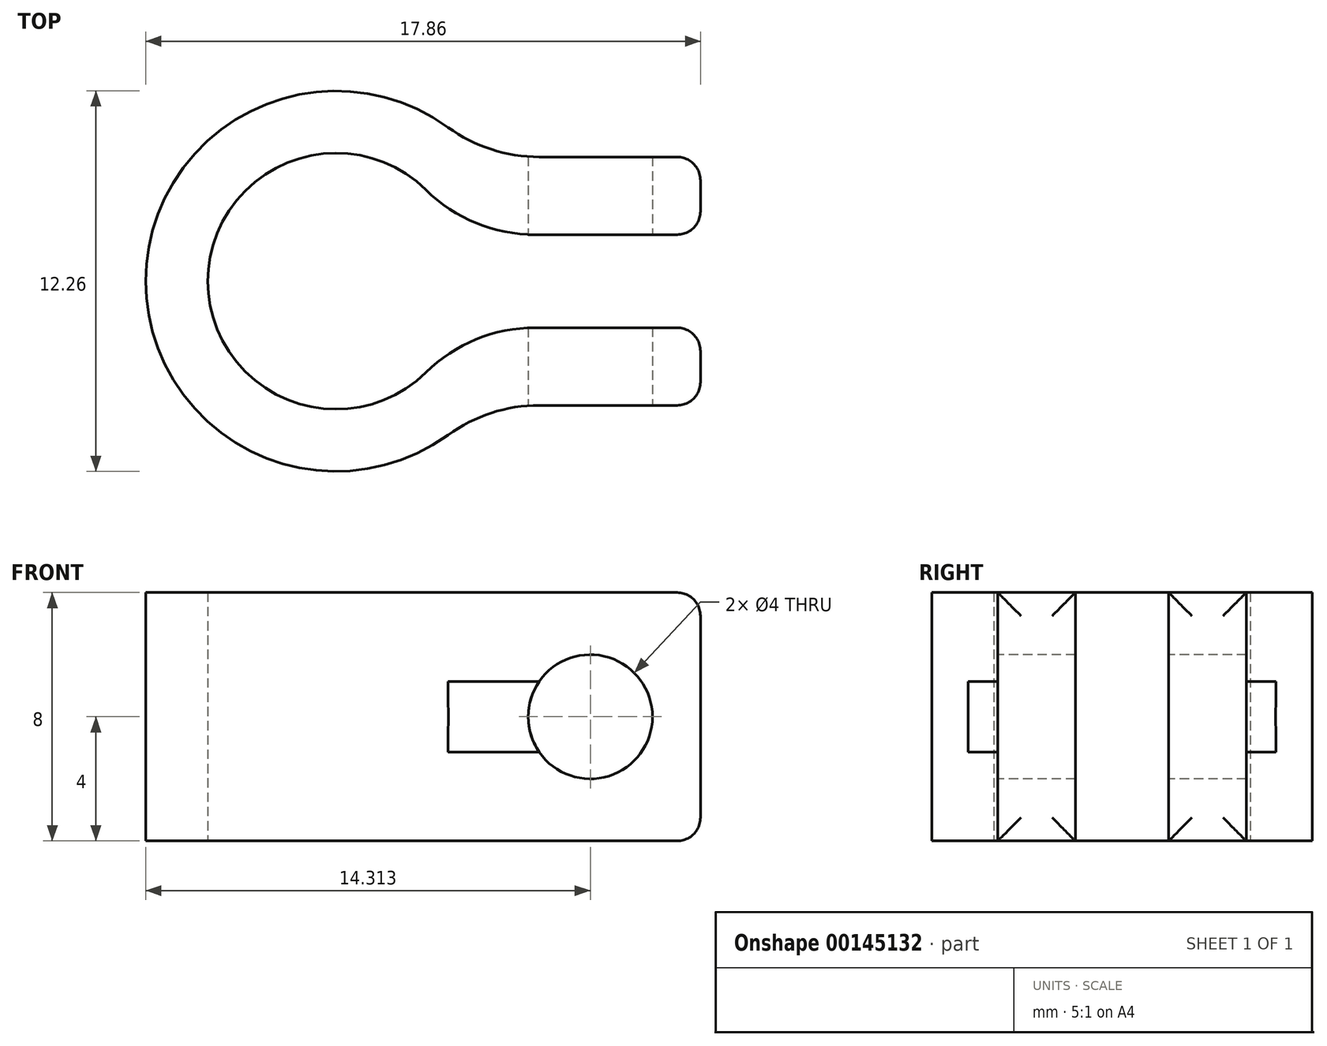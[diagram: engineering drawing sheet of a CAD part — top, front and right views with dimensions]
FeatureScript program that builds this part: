
annotation { "Feature Type Name" : "Feature", "Feature Type Description" : "" }
export const myFeature = defineFeature(function(context is Context, id is Id, definition is map)
    precondition{}
    {
        {
            var Q0;
            Q0=qCreatedBy(makeId("Top.planeOp"),FACE);
            var sketch = newSketch(context, id + "F0", { "sketchPlane" : qUnion([Q0])});
            skCircle(sketch, "E0", {"center": v(0, 0) * mm, "radius": 4.12 * mm});
            skCircle(sketch, "E1", {"center": v(0, 0) * mm, "radius": 6.12 * mm});
            skLineSegment(sketch, "E2.bottom", {"start": v(4.64, -4) * mm, "end": v(11.73, -4) * mm});
            skLineSegment(sketch, "E2.top", {"start": v(4.64, 4) * mm, "end": v(11.73, 4) * mm});
            skLineSegment(sketch, "E2.right", {"start": v(11.73, -4) * mm, "end": v(11.73, 4) * mm});
            skLineSegment(sketch, "E3", {"start": v(11.73, 0) * mm, "end": v(4.12, 0) * mm, "construction": true});
            skLineSegment(sketch, "E4.0", {"start": v(11.73, 1.5) * mm, "end": v(3.84, 1.5) * mm});
            skLineSegment(sketch, "E5.0", {"start": v(11.73, -1.5) * mm, "end": v(3.84, -1.5) * mm});
            skSolve(sketch);
        }
        {
            var Q0;
            {var subQ0=sQuery(id+"F0.wireOp",EDGE,"E2.top");Q0=makeQuery(id+"F0.imprint","IMPRINT",FACE,{"disambiguationData":[TD([[makeQuery(id+"F0.imprint","IMPRINT",EDGE,{"derivedFrom":subQ0}),-1.0]])]});}
            var Q1;
            {var subQ0=sQuery(id+"F0.wireOp",EDGE,"E2.bottom");Q1=makeQuery(id+"F0.imprint","IMPRINT",FACE,{"disambiguationData":[TD([[makeQuery(id+"F0.imprint","IMPRINT",EDGE,{"derivedFrom":subQ0}),1.0]])]});}
            var Q2;
            {var subQ5=sQuery(id+"F0.wireOp",EDGE,"E4.0");var subQ7=sQuery(id+"F0.wireOp",EDGE,"E0");var subQ8=makeQuery(id+"F0.imprint","INTERSECT",VERTEX,{"derivedFrom":[subQ7,subQ5]});Q2=makeQuery(id+"F0.imprint","IMPRINT",FACE,{"disambiguationData":[TD([[makeQuery(id+"F0.imprint","IMPRINT",EDGE,{"disambiguationData":[TD([[subQ8,-1.0]])],"derivedFrom":subQ7}),-1.0]])]});}
            extrude(context, id + "F1", {"entities" : qUnion([Q0, Q1, Q2]), "depth" : 8 * mm});
        }
        {
            var Q0;
            Q0=makeQuery(id+"F1.opExtrude","SWEPT_FACE",FACE,{"disambiguationData":[OSD([sQuery(id+"F0.wireOp",EDGE,"E2.bottom")])]});
            var sketch = newSketch(context, id + "F2", { "sketchPlane" : qUnion([Q0])});
            skCircle(sketch, "E6", {"center": v(8.18, 4) * mm, "radius": 2 * mm});
            skPoint(sketch, "E6.centerSnap0", {"position": v(8.18, 8) * mm});
            skPoint(sketch, "E6.centerSnap1", {"position": v(11.73, 4) * mm});
            skSolve(sketch);
        }
        {
            var Q0;
            Q0 = qSketchRegion(id + "F2", true);
            extrude(context, id + "F3", {"entities" : qUnion([Q0]), "operationType" : NewBodyOperationType.REMOVE, "oppositeDirection" : true, "depth" : 25 * mm});
        }
        {
            var Q0;
            {var subQ0=sQuery(id+"F0.wireOp",EDGE,"E2.right");Q0=makeQuery(id+"F1.opExtrude","CAP_EDGE",EDGE,{"disambiguationData":[OSD([subQ0]),TDD([makeQuery(id+"F0.imprint","IMPRINT",EDGE,{"disambiguationData":[TD([[makeQuery(id+"F0.imprint","INTERSECT",VERTEX,{"derivedFrom":[sQuery(id+"F0.wireOp",EDGE,"E2.bottom"),subQ0]}),-1.0]])],"derivedFrom":subQ0})])],"isStart":false});}
            var Q1;
            {var subQ0=sQuery(id+"F0.wireOp",EDGE,"E2.right");Q1=makeQuery(id+"F1.opExtrude","CAP_EDGE",EDGE,{"disambiguationData":[OSD([subQ0]),TDD([makeQuery(id+"F0.imprint","IMPRINT",EDGE,{"disambiguationData":[TD([[makeQuery(id+"F0.imprint","INTERSECT",VERTEX,{"derivedFrom":[sQuery(id+"F0.wireOp",EDGE,"E2.top"),subQ0]}),1.0]])],"derivedFrom":subQ0})])],"isStart":false});}
            var Q2;
            {var subQ0=sQuery(id+"F0.wireOp",EDGE,"E2.right");Q2=makeQuery(id+"F1.opExtrude","CAP_EDGE",EDGE,{"disambiguationData":[OSD([subQ0]),TDD([makeQuery(id+"F0.imprint","IMPRINT",EDGE,{"disambiguationData":[TD([[makeQuery(id+"F0.imprint","INTERSECT",VERTEX,{"derivedFrom":[sQuery(id+"F0.wireOp",EDGE,"E2.bottom"),subQ0]}),-1.0]])],"derivedFrom":subQ0})])],"isStart":true});}
            var Q3;
            {var subQ0=sQuery(id+"F0.wireOp",EDGE,"E2.right");Q3=makeQuery(id+"F1.opExtrude","CAP_EDGE",EDGE,{"disambiguationData":[OSD([subQ0]),TDD([makeQuery(id+"F0.imprint","IMPRINT",EDGE,{"disambiguationData":[TD([[makeQuery(id+"F0.imprint","INTERSECT",VERTEX,{"derivedFrom":[sQuery(id+"F0.wireOp",EDGE,"E2.top"),subQ0]}),1.0]])],"derivedFrom":subQ0})])],"isStart":true});}
            var Q4;
            Q4=makeQuery(id+"F1.opExtrude","SWEPT_EDGE",EDGE,{"disambiguationData":[OSD([sQuery(id+"F0.wireOp",EDGE,"E2.top"),sQuery(id+"F0.wireOp",EDGE,"E2.right")])]});
            var Q5;
            Q5=makeQuery(id+"F1.opExtrude","SWEPT_EDGE",EDGE,{"disambiguationData":[OSD([sQuery(id+"F0.wireOp",EDGE,"E2.right"),sQuery(id+"F0.wireOp",EDGE,"E4.0")])]});
            var Q6;
            Q6=makeQuery(id+"F1.opExtrude","SWEPT_EDGE",EDGE,{"disambiguationData":[OSD([sQuery(id+"F0.wireOp",EDGE,"E2.right"),sQuery(id+"F0.wireOp",EDGE,"E5.0")])]});
            var Q7;
            Q7=makeQuery(id+"F1.opExtrude","SWEPT_EDGE",EDGE,{"disambiguationData":[OSD([sQuery(id+"F0.wireOp",EDGE,"E2.bottom"),sQuery(id+"F0.wireOp",EDGE,"E2.right")])]});
            fillet(context, id + "F4", {"entities" : qUnion([Q0, Q1, Q2, Q3, Q4, Q5, Q6, Q7]), "radius" : .75 * mm, "tangentPropagation" : true, "allowEdgeOverflow" : false});
        }
        {
            var Q0;
            Q0=makeQuery(id+"F1.opExtrude","SWEPT_EDGE",EDGE,{"disambiguationData":[OSD([sQuery(id+"F0.wireOp",EDGE,"E0"),sQuery(id+"F0.wireOp",EDGE,"E4.0")])]});
            var Q1;
            Q1=makeQuery(id+"F1.opExtrude","SWEPT_EDGE",EDGE,{"disambiguationData":[OSD([sQuery(id+"F0.wireOp",EDGE,"E0"),sQuery(id+"F0.wireOp",EDGE,"E5.0")])]});
            var Q2;
            Q2=makeQuery(id+"F1.opExtrude","SWEPT_EDGE",EDGE,{"disambiguationData":[OSD([sQuery(id+"F0.wireOp",EDGE,"E1"),sQuery(id+"F0.wireOp",EDGE,"E2.bottom")])]});
            var Q3;
            Q3=makeQuery(id+"F1.opExtrude","SWEPT_EDGE",EDGE,{"disambiguationData":[OSD([sQuery(id+"F0.wireOp",EDGE,"E1"),sQuery(id+"F0.wireOp",EDGE,"E2.top")])]});
            fillet(context, id + "F5", {"entities" : qUnion([Q0, Q1, Q2, Q3]), "radius" : 5 * mm, "tangentPropagation" : true, "allowEdgeOverflow" : false});
        }
    });
